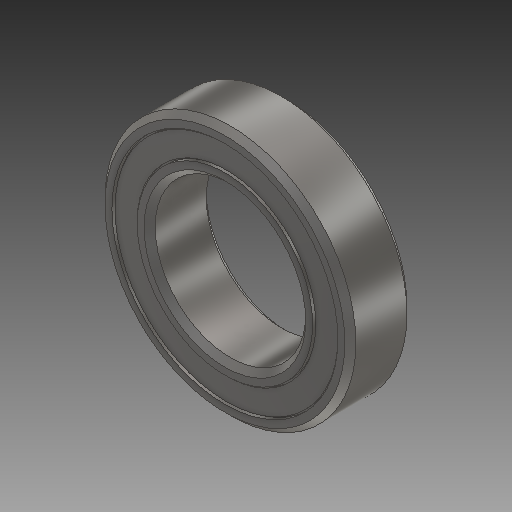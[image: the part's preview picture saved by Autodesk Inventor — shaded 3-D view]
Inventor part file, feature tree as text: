
AUTODESK INVENTOR PART (.ipt)
format: ipt  version: 2018.2 (Build 222227000, 227)  size: 208,896 bytes
history: native  units: mm
features: revolve x1, chamfer x1, sketch x1
ambient origin geometry x8: Origin, YZ Plane, XZ Plane, XY Plane, X Axis, Y Axis, Z Axis, Center Point
bodies: Solid1 (feature_tree)
feature tree (3):
  revolve  "Revolution1"  [1 undecoded]
  chamfer  "Chamfer1"  Distance=15.875mm
  sketch  "Sketch1"  dims[d0=9.525mm d1=3.937mm d2=15.875mm d3=0.1mm d4=0.25mm d5=0.1mm d6=0.1mm d7=1.4mm d8=0.2mm d9=90.0deg d10=0.35mm d11=2.0mm d12=45.0deg]
note: 1 required parameter value undecoded (feature->parameter linkage not recoverable at this tier; creation-order binding heuristic only, values carry confidence <= 0.55)
